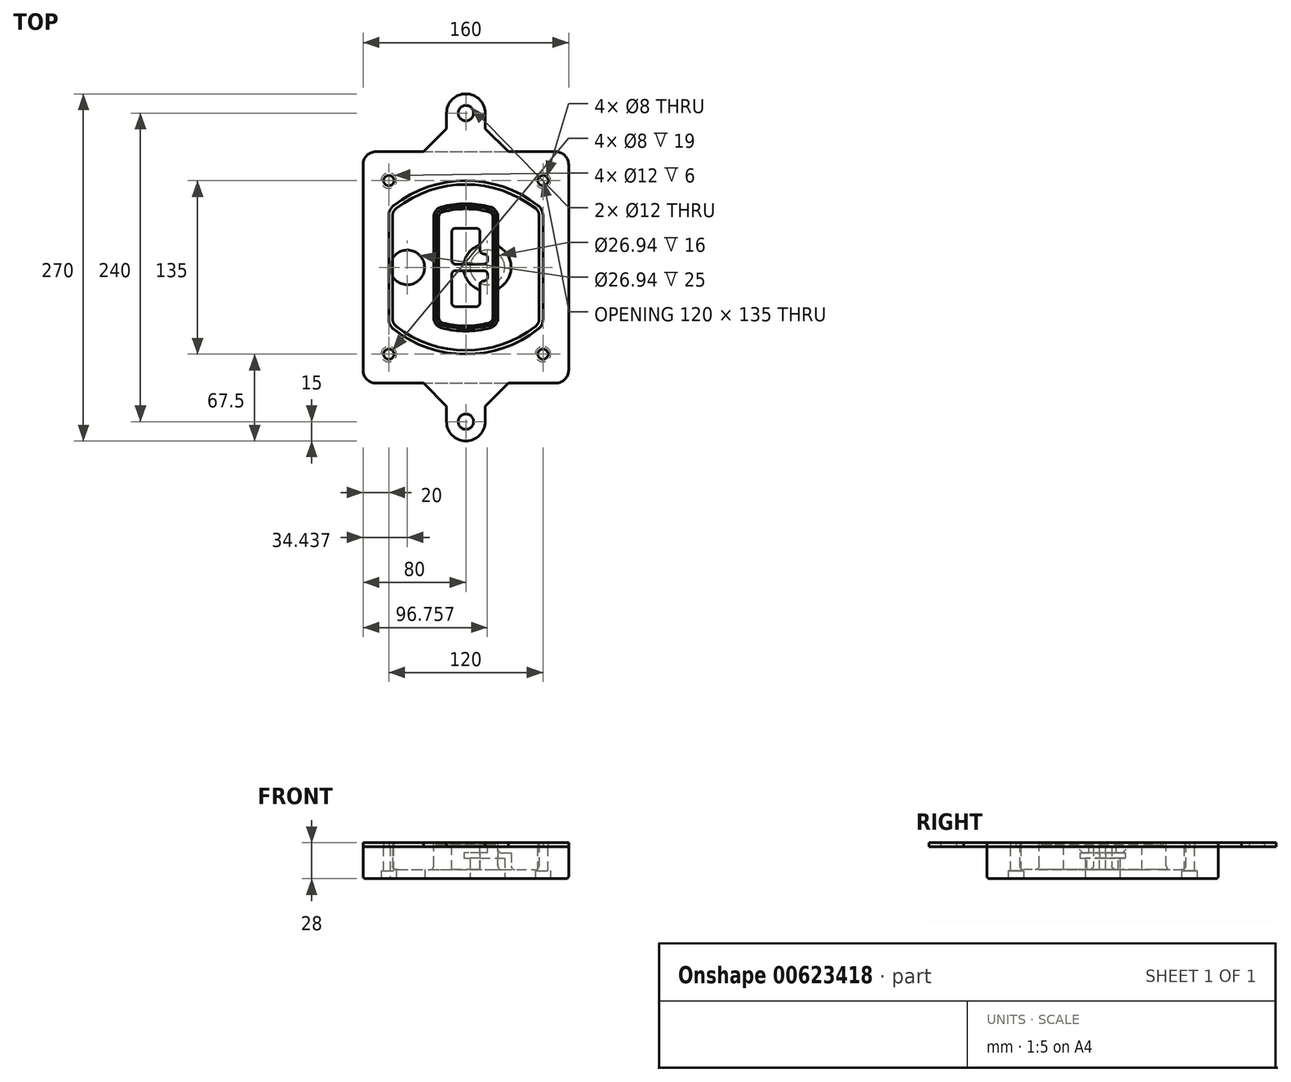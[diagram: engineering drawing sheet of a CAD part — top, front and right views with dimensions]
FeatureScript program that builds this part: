
annotation { "Feature Type Name" : "Feature", "Feature Type Description" : "" }
export const myFeature = defineFeature(function(context is Context, id is Id, definition is map)
    precondition{}
    {
        {
            var Q0;
            Q0=qCreatedBy(makeId("Top.planeOp"),FACE);
            var sketch = newSketch(context, id + "F0", { "sketchPlane" : qUnion([Q0])});
            skPoint(sketch, "E0.rect.middle", {"position": v(0, 0) * mm});
            skLineSegment(sketch, "E1.bottom", {"start": v(-70, -90) * mm, "end": v(70, -90) * mm});
            skLineSegment(sketch, "E1.top", {"start": v(-70, 90) * mm, "end": v(70, 90) * mm});
            skLineSegment(sketch, "E1.left", {"start": v(-80, -80) * mm, "end": v(-80, 80) * mm});
            skLineSegment(sketch, "E1.right", {"start": v(80, -80) * mm, "end": v(80, 80) * mm});
            skLineSegment(sketch, "E2", {"start": v(-80, 90) * mm, "end": v(80, -90) * mm, "construction": true});
            skLineSegment(sketch, "E3", {"start": v(80, 90) * mm, "end": v(-80, -90) * mm, "construction": true});
            skCircle(sketch, "E4", {"center": v(-60, 67.5) * mm, "radius": 4 * mm});
            skCircle(sketch, "E5", {"center": v(60, 67.5) * mm, "radius": 4 * mm});
            skCircle(sketch, "E6", {"center": v(60, -67.5) * mm, "radius": 4 * mm});
            skCircle(sketch, "E7", {"center": v(-60, -67.5) * mm, "radius": 4 * mm});
            skLineSegment(sketch, "E8", {"start": v(-60, 67.5) * mm, "end": v(60, 67.5) * mm, "construction": true});
            skLineSegment(sketch, "E9", {"start": v(60, 67.5) * mm, "end": v(60, -67.5) * mm, "construction": true});
            skLineSegment(sketch, "E10", {"start": v(60, -67.5) * mm, "end": v(-60, -67.5) * mm, "construction": true});
            skLineSegment(sketch, "E11", {"start": v(-60, -67.5) * mm, "end": v(-60, 67.5) * mm, "construction": true});
            skLineSegment(sketch, "E12", {"start": v(-60, 40.3) * mm, "end": v(-60, -40.3) * mm});
            skLineSegment(sketch, "E13", {"start": v(60, 40.3) * mm, "end": v(60, -40.3) * mm});
            skArc(sketch, "E14", {"start": v(56.15, 48.18) * mm, "mid": v(0, 67.5) * mm, "end": v(-56.15, 48.18) * mm});
            skArc(sketch, "E15", {"start": v(-56.15, -48.18) * mm, "mid": v(0, -67.5) * mm, "end": v(56.15, -48.18) * mm});
            skLineSegment(sketch, "E16", {"start": v(-60, 0) * mm, "end": v(60, 0) * mm, "construction": true});
            skPoint(sketch, "E17.visualSharp", {"position": v(-60, -45) * mm});
            skArc(sketch, "E17.filletArc", {"start": v(-60, -40.3) * mm, "mid": v(-58.99, -44.68) * mm, "end": v(-56.15, -48.18) * mm});
            skPoint(sketch, "E18.visualSharp", {"position": v(-60, 45) * mm});
            skArc(sketch, "E18.filletArc", {"start": v(-56.15, 48.18) * mm, "mid": v(-58.99, 44.68) * mm, "end": v(-60, 40.3) * mm});
            skPoint(sketch, "E19.visualSharp", {"position": v(60, 45) * mm});
            skArc(sketch, "E19.filletArc", {"start": v(60, 40.3) * mm, "mid": v(58.99, 44.68) * mm, "end": v(56.15, 48.18) * mm});
            skPoint(sketch, "E20.visualSharp", {"position": v(60, -45) * mm});
            skArc(sketch, "E20.filletArc", {"start": v(56.15, -48.18) * mm, "mid": v(58.99, -44.68) * mm, "end": v(60, -40.3) * mm});
            skPoint(sketch, "E21.visualSharp", {"position": v(-80, 90) * mm});
            skArc(sketch, "E21.filletArc", {"start": v(-70, 90) * mm, "mid": v(-77.07, 87.07) * mm, "end": v(-80, 80) * mm});
            skPoint(sketch, "E22.visualSharp", {"position": v(80, 90) * mm});
            skArc(sketch, "E22.filletArc", {"start": v(80, 80) * mm, "mid": v(77.07, 87.07) * mm, "end": v(70, 90) * mm});
            skPoint(sketch, "E23.visualSharp", {"position": v(80, -90) * mm});
            skArc(sketch, "E23.filletArc", {"start": v(70, -90) * mm, "mid": v(77.07, -87.07) * mm, "end": v(80, -80) * mm});
            skPoint(sketch, "E24.visualSharp", {"position": v(-80, -90) * mm});
            skArc(sketch, "E24.filletArc", {"start": v(-80, -80) * mm, "mid": v(-77.07, -87.07) * mm, "end": v(-70, -90) * mm});
            skArc(sketch, "E25.0", {"start": v(57, 40.3) * mm, "mid": v(56.3, 43.36) * mm, "end": v(54.3, 45.81) * mm});
            skLineSegment(sketch, "E25.1", {"start": v(57, 40.3) * mm, "end": v(57, -40.3) * mm});
            skArc(sketch, "E25.2", {"start": v(54.3, -45.81) * mm, "mid": v(56.3, -43.36) * mm, "end": v(57, -40.3) * mm});
            skArc(sketch, "E25.3", {"start": v(-54.3, -45.81) * mm, "mid": v(0, -64.5) * mm, "end": v(54.3, -45.81) * mm});
            skArc(sketch, "E25.4", {"start": v(-57, -40.3) * mm, "mid": v(-56.3, -43.36) * mm, "end": v(-54.3, -45.81) * mm});
            skArc(sketch, "E25.5", {"start": v(54.3, 45.81) * mm, "mid": v(0, 64.5) * mm, "end": v(-54.3, 45.81) * mm});
            skLineSegment(sketch, "E25.6", {"start": v(-57, 40.3) * mm, "end": v(-57, -40.3) * mm});
            skArc(sketch, "E25.7", {"start": v(-54.3, 45.81) * mm, "mid": v(-56.3, 43.36) * mm, "end": v(-57, 40.3) * mm});
            skArc(sketch, "E26.0", {"start": v(-58.62, 51.33) * mm, "mid": v(-62.58, 46.43) * mm, "end": v(-64, 40.3) * mm});
            skArc(sketch, "E26.1", {"start": v(58.62, 51.33) * mm, "mid": v(0, 71.5) * mm, "end": v(-58.62, 51.33) * mm});
            skArc(sketch, "E26.2", {"start": v(64, 40.3) * mm, "mid": v(62.58, 46.43) * mm, "end": v(58.62, 51.33) * mm});
            skLineSegment(sketch, "E26.3", {"start": v(64, 40.3) * mm, "end": v(64, -40.3) * mm});
            skArc(sketch, "E26.4", {"start": v(58.62, -51.33) * mm, "mid": v(62.58, -46.43) * mm, "end": v(64, -40.3) * mm});
            skLineSegment(sketch, "E26.5", {"start": v(-64, 40.3) * mm, "end": v(-64, -40.3) * mm});
            skArc(sketch, "E26.6", {"start": v(-58.62, -51.33) * mm, "mid": v(0, -71.5) * mm, "end": v(58.62, -51.33) * mm});
            skArc(sketch, "E26.7", {"start": v(-64, -40.3) * mm, "mid": v(-62.58, -46.43) * mm, "end": v(-58.62, -51.33) * mm});
            skSolve(sketch);
        }
        {
            var Q0;
            Q0=makeQuery(id+"F0.imprint","IMPRINT",FACE,{"disambiguationData":[TD([[makeQuery(id+"F0.imprint","IMPRINT",EDGE,{"derivedFrom":sQuery(id+"F0.wireOp",EDGE,"E1.bottom")}),1.0]])]});
            var Q1;
            Q1=makeQuery(id+"F0.imprint","IMPRINT",FACE,{"disambiguationData":[TD([[makeQuery(id+"F0.imprint","IMPRINT",EDGE,{"derivedFrom":sQuery(id+"F0.wireOp",EDGE,"E12")}),1.0]])]});
            var Q2;
            Q2=makeQuery(id+"F0.imprint","IMPRINT",FACE,{"disambiguationData":[TD([[makeQuery(id+"F0.imprint","IMPRINT",EDGE,{"derivedFrom":sQuery(id+"F0.wireOp",EDGE,"E25.0")}),1.0]])]});
            var Q3;
            Q3=makeQuery(id+"F0.imprint","IMPRINT",FACE,{"disambiguationData":[TD([[makeQuery(id+"F0.imprint","IMPRINT",EDGE,{"derivedFrom":sQuery(id+"F0.wireOp",EDGE,"E12")}),-1.0]])]});
            extrude(context, id + "F1", {"entities" : qUnion([Q0, Q1, Q2, Q3]), "oppositeDirection" : true, "depth" : 25 * mm});
        }
        {
            var Q0;
            Q0=makeQuery(id+"F0.imprint","IMPRINT",FACE,{"disambiguationData":[TD([[makeQuery(id+"F0.imprint","IMPRINT",EDGE,{"derivedFrom":sQuery(id+"F0.wireOp",EDGE,"E12")}),1.0]])]});
            extrude(context, id + "F2", {"entities" : qUnion([Q0]), "operationType" : NewBodyOperationType.ADD, "depth" : 3 * mm});
        }
        {
            var Q0;
            Q0=makeQuery(id+"F0.imprint","IMPRINT",FACE,{"disambiguationData":[TD([[makeQuery(id+"F0.imprint","IMPRINT",EDGE,{"derivedFrom":sQuery(id+"F0.wireOp",EDGE,"E25.0")}),1.0]])]});
            extrude(context, id + "F3", {"entities" : qUnion([Q0]), "operationType" : NewBodyOperationType.REMOVE, "oppositeDirection" : true, "depth" : 18 * mm});
        }
        {
            var Q0;
            Q0=makeQuery(id+"F2.opExtrude","CAP_FACE",FACE,{"disambiguationData":[OSD([sQuery(id+"F0.wireOp",EDGE,"E12"),sQuery(id+"F0.wireOp",EDGE,"E13"),sQuery(id+"F0.wireOp",EDGE,"E14"),sQuery(id+"F0.wireOp",EDGE,"E15"),sQuery(id+"F0.wireOp",EDGE,"E17.filletArc"),sQuery(id+"F0.wireOp",EDGE,"E18.filletArc"),sQuery(id+"F0.wireOp",EDGE,"E19.filletArc"),sQuery(id+"F0.wireOp",EDGE,"E20.filletArc"),sQuery(id+"F0.wireOp",EDGE,"E25.0"),sQuery(id+"F0.wireOp",EDGE,"E25.1"),sQuery(id+"F0.wireOp",EDGE,"E25.2"),sQuery(id+"F0.wireOp",EDGE,"E25.3"),sQuery(id+"F0.wireOp",EDGE,"E25.4"),sQuery(id+"F0.wireOp",EDGE,"E25.5"),sQuery(id+"F0.wireOp",EDGE,"E25.6"),sQuery(id+"F0.wireOp",EDGE,"E25.7")])],"isStart":false});
            var sketch = newSketch(context, id + "F4", { "sketchPlane" : qUnion([Q0])});
            skArc(sketch, "E27.0", {"start": v(-19.08, -46.97) * mm, "mid": v(0, -49.5) * mm, "end": v(19.08, -46.97) * mm});
            skArc(sketch, "E28.0", {"start": v(19.08, 46.97) * mm, "mid": v(0, 49.5) * mm, "end": v(-19.08, 46.97) * mm});
            skLineSegment(sketch, "E29", {"start": v(-25, 39.25) * mm, "end": v(-25, -39.25) * mm});
            skLineSegment(sketch, "E30", {"start": v(25, 39.25) * mm, "end": v(25, -39.25) * mm});
            skLineSegment(sketch, "E31", {"start": v(-25, 45.1) * mm, "end": v(25, 45.1) * mm, "construction": true});
            skLineSegment(sketch, "E32", {"start": v(-25, -45.1) * mm, "end": v(25, -45.1) * mm, "construction": true});
            skPoint(sketch, "E33.visualSharp", {"position": v(-25, 45.1) * mm});
            skArc(sketch, "E33.filletArc", {"start": v(-19.08, 46.97) * mm, "mid": v(-23.35, 44.11) * mm, "end": v(-25, 39.25) * mm});
            skPoint(sketch, "E34.visualSharp", {"position": v(25, 45.1) * mm});
            skArc(sketch, "E34.filletArc", {"start": v(25, 39.25) * mm, "mid": v(23.35, 44.11) * mm, "end": v(19.08, 46.97) * mm});
            skPoint(sketch, "E35.visualSharp", {"position": v(25, -45.1) * mm});
            skArc(sketch, "E35.filletArc", {"start": v(19.08, -46.97) * mm, "mid": v(23.35, -44.11) * mm, "end": v(25, -39.25) * mm});
            skPoint(sketch, "E36.visualSharp", {"position": v(-25, -45.1) * mm});
            skArc(sketch, "E36.filletArc", {"start": v(-25, -39.25) * mm, "mid": v(-23.35, -44.11) * mm, "end": v(-19.08, -46.97) * mm});
            skArc(sketch, "E37.0", {"start": v(54.3, 45.81) * mm, "mid": v(0, 64.5) * mm, "end": v(-54.3, 45.81) * mm});
            skArc(sketch, "E37.1", {"start": v(-54.3, 45.81) * mm, "mid": v(-56.3, 43.36) * mm, "end": v(-57, 40.3) * mm});
            skLineSegment(sketch, "E37.2", {"start": v(-57, 40.3) * mm, "end": v(-57, -40.3) * mm});
            skArc(sketch, "E37.3", {"start": v(-57, -40.3) * mm, "mid": v(-56.3, -43.36) * mm, "end": v(-54.3, -45.81) * mm});
            skArc(sketch, "E37.4", {"start": v(-54.3, -45.81) * mm, "mid": v(0, -64.5) * mm, "end": v(54.3, -45.81) * mm});
            skArc(sketch, "E37.5", {"start": v(54.3, -45.81) * mm, "mid": v(56.3, -43.36) * mm, "end": v(57, -40.3) * mm});
            skLineSegment(sketch, "E37.6", {"start": v(57, 40.3) * mm, "end": v(57, -40.3) * mm});
            skArc(sketch, "E37.7", {"start": v(57, 40.3) * mm, "mid": v(56.3, 43.36) * mm, "end": v(54.3, 45.81) * mm});
            skLineSegment(sketch, "E38.0", {"start": v(23, 39.25) * mm, "end": v(23, -39.25) * mm});
            skArc(sketch, "E38.1", {"start": v(18.56, -45.04) * mm, "mid": v(21.76, -42.9) * mm, "end": v(23, -39.25) * mm});
            skArc(sketch, "E38.2", {"start": v(-18.56, -45.04) * mm, "mid": v(0, -47.5) * mm, "end": v(18.56, -45.04) * mm});
            skArc(sketch, "E38.3", {"start": v(-23, -39.25) * mm, "mid": v(-21.76, -42.9) * mm, "end": v(-18.56, -45.04) * mm});
            skLineSegment(sketch, "E38.4", {"start": v(-23, 39.25) * mm, "end": v(-23, -39.25) * mm});
            skArc(sketch, "E38.5", {"start": v(23, 39.25) * mm, "mid": v(21.76, 42.9) * mm, "end": v(18.56, 45.04) * mm});
            skArc(sketch, "E38.6", {"start": v(-18.56, 45.04) * mm, "mid": v(-21.76, 42.9) * mm, "end": v(-23, 39.25) * mm});
            skArc(sketch, "E38.7", {"start": v(18.56, 45.04) * mm, "mid": v(0, 47.5) * mm, "end": v(-18.56, 45.04) * mm});
            skArc(sketch, "E39.0", {"start": v(21, 39.25) * mm, "mid": v(20.18, 41.68) * mm, "end": v(18.04, 43.1) * mm});
            skLineSegment(sketch, "E39.1", {"start": v(21, 39.25) * mm, "end": v(21, -39.25) * mm});
            skArc(sketch, "E39.2", {"start": v(18.04, -43.1) * mm, "mid": v(20.18, -41.68) * mm, "end": v(21, -39.25) * mm});
            skArc(sketch, "E39.3", {"start": v(-18.04, -43.1) * mm, "mid": v(0, -45.5) * mm, "end": v(18.04, -43.1) * mm});
            skArc(sketch, "E39.4", {"start": v(-21, -39.25) * mm, "mid": v(-20.18, -41.68) * mm, "end": v(-18.04, -43.1) * mm});
            skArc(sketch, "E39.5", {"start": v(18.04, 43.1) * mm, "mid": v(0, 45.5) * mm, "end": v(-18.04, 43.1) * mm});
            skLineSegment(sketch, "E39.6", {"start": v(-21, 39.25) * mm, "end": v(-21, -39.25) * mm});
            skArc(sketch, "E39.7", {"start": v(-18.04, 43.1) * mm, "mid": v(-20.18, 41.68) * mm, "end": v(-21, 39.25) * mm});
            skLineSegment(sketch, "E40", {"start": v(-25, 0) * mm, "end": v(25, 0) * mm, "construction": true});
            skLineSegment(sketch, "E41", {"start": v(-11, 5.5) * mm, "end": v(-11, 27.5) * mm});
            skLineSegment(sketch, "E42", {"start": v(-8, 30.5) * mm, "end": v(8, 30.5) * mm});
            skLineSegment(sketch, "E43", {"start": v(11, 27.5) * mm, "end": v(11, 13.5) * mm});
            skLineSegment(sketch, "E44", {"start": v(14, 10.5) * mm, "end": v(14, 10.5) * mm});
            skLineSegment(sketch, "E45", {"start": v(17, 7.5) * mm, "end": v(17, 5.5) * mm});
            skLineSegment(sketch, "E46", {"start": v(14, 2.5) * mm, "end": v(-8, 2.5) * mm});
            skPoint(sketch, "E47.visualSharp", {"position": v(-11, 30.5) * mm});
            skArc(sketch, "E47.filletArc", {"start": v(-8, 30.5) * mm, "mid": v(-10.12, 29.62) * mm, "end": v(-11, 27.5) * mm});
            skPoint(sketch, "E48.visualSharp", {"position": v(11, 30.5) * mm});
            skArc(sketch, "E48.filletArc", {"start": v(11, 27.5) * mm, "mid": v(10.12, 29.62) * mm, "end": v(8, 30.5) * mm});
            skPoint(sketch, "E49.visualSharp", {"position": v(11, 10.5) * mm});
            skArc(sketch, "E49.filletArc", {"start": v(11, 13.5) * mm, "mid": v(11.88, 11.38) * mm, "end": v(14, 10.5) * mm});
            skPoint(sketch, "E50.visualSharp", {"position": v(17, 10.5) * mm});
            skArc(sketch, "E50.filletArc", {"start": v(17, 7.5) * mm, "mid": v(16.12, 9.62) * mm, "end": v(14, 10.5) * mm});
            skPoint(sketch, "E51.visualSharp", {"position": v(17, 2.5) * mm});
            skArc(sketch, "E51.filletArc", {"start": v(14, 2.5) * mm, "mid": v(16.12, 3.38) * mm, "end": v(17, 5.5) * mm});
            skPoint(sketch, "E52.visualSharp", {"position": v(-11, 2.5) * mm});
            skArc(sketch, "E52.filletArc", {"start": v(-11, 5.5) * mm, "mid": v(-10.12, 3.38) * mm, "end": v(-8, 2.5) * mm});
            skLineSegment(sketch, "E53.0.MirrorCS", {"start": v(14, -2.5) * mm, "end": v(-8, -2.5) * mm});
            skArc(sketch, "E54.0.MirrorCS", {"start": v(-11, -5.5) * mm, "mid": v(-10.12, -3.38) * mm, "end": v(-8, -2.5) * mm});
            skLineSegment(sketch, "E55.0.MirrorCS", {"start": v(-11, -5.5) * mm, "end": v(-11, -27.5) * mm});
            skArc(sketch, "E56.0.MirrorCS", {"start": v(-8, -30.5) * mm, "mid": v(-10.12, -29.62) * mm, "end": v(-11, -27.5) * mm});
            skLineSegment(sketch, "E57.0.MirrorCS", {"start": v(-8, -30.5) * mm, "end": v(8, -30.5) * mm});
            skArc(sketch, "E58.0.MirrorCS", {"start": v(11, -27.5) * mm, "mid": v(10.12, -29.62) * mm, "end": v(8, -30.5) * mm});
            skLineSegment(sketch, "E59.0.MirrorCS", {"start": v(11, -27.5) * mm, "end": v(11, -13.5) * mm});
            skArc(sketch, "E60.0.MirrorCS", {"start": v(11, -13.5) * mm, "mid": v(11.88, -11.38) * mm, "end": v(14, -10.5) * mm});
            skArc(sketch, "E61.0.MirrorCS", {"start": v(17, -7.5) * mm, "mid": v(16.12, -9.62) * mm, "end": v(14, -10.5) * mm});
            skLineSegment(sketch, "E62.0.MirrorCS", {"start": v(17, -7.5) * mm, "end": v(17, -5.5) * mm});
            skArc(sketch, "E63.0.MirrorCS", {"start": v(14, -2.5) * mm, "mid": v(16.12, -3.38) * mm, "end": v(17, -5.5) * mm});
            skSolve(sketch);
        }
        {
            var Q0;
            Q0=makeQuery(id+"F4.imprint","IMPRINT",FACE,{"disambiguationData":[TD([[makeQuery(id+"F4.imprint","IMPRINT",EDGE,{"derivedFrom":sQuery(id+"F4.wireOp",EDGE,"E27.0")}),1.0]])]});
            var Q1;
            Q1=makeQuery(id+"F4.imprint","IMPRINT",FACE,{"disambiguationData":[TD([[makeQuery(id+"F4.imprint","IMPRINT",EDGE,{"derivedFrom":sQuery(id+"F4.wireOp",EDGE,"E38.0")}),-1.0]])]});
            var Q2;
            Q2=makeQuery(id+"F4.imprint","IMPRINT",FACE,{"disambiguationData":[TD([[makeQuery(id+"F4.imprint","IMPRINT",EDGE,{"derivedFrom":sQuery(id+"F4.wireOp",EDGE,"E39.0")}),1.0]])]});
            extrude(context, id + "F5", {"entities" : qUnion([Q0, Q1, Q2]), "operationType" : NewBodyOperationType.ADD, "endBound" : BoundingType.UP_TO_NEXT, "oppositeDirection" : true, "depth" : 25 * mm});
        }
        {
            var Q0;
            Q0=makeQuery(id+"F4.imprint","IMPRINT",FACE,{"disambiguationData":[TD([[makeQuery(id+"F4.imprint","IMPRINT",EDGE,{"derivedFrom":sQuery(id+"F4.wireOp",EDGE,"E38.0")}),-1.0]])]});
            extrude(context, id + "F6", {"entities" : qUnion([Q0]), "operationType" : NewBodyOperationType.REMOVE, "oppositeDirection" : true, "depth" : 2 * mm});
        }
        {
            var Q0;
            Q0=makeQuery(id+"F1.opExtrude","CAP_FACE",FACE,{"disambiguationData":[OSD([sQuery(id+"F0.wireOp",EDGE,"E1.bottom"),sQuery(id+"F0.wireOp",EDGE,"E1.top"),sQuery(id+"F0.wireOp",EDGE,"E1.left"),sQuery(id+"F0.wireOp",EDGE,"E1.right"),sQuery(id+"F0.wireOp",EDGE,"E4"),sQuery(id+"F0.wireOp",EDGE,"E5"),sQuery(id+"F0.wireOp",EDGE,"E6"),sQuery(id+"F0.wireOp",EDGE,"E7"),sQuery(id+"F0.wireOp",EDGE,"E21.filletArc"),sQuery(id+"F0.wireOp",EDGE,"E22.filletArc"),sQuery(id+"F0.wireOp",EDGE,"E23.filletArc"),sQuery(id+"F0.wireOp",EDGE,"E24.filletArc")])],"isStart":false});
            var sketch = newSketch(context, id + "F7", { "sketchPlane" : qUnion([Q0])});
            skCircle(sketch, "E64", {"center": v(16.76, 0) * mm, "radius": 13.47 * mm});
            skCircle(sketch, "E65", {"center": v(-45.56, 0) * mm, "radius": 13.47 * mm});
            skLineSegment(sketch, "E66", {"start": v(80, 0) * mm, "end": v(-80, 0) * mm});
            skCircle(sketch, "E67", {"center": v(16.76, 0) * mm, "radius": 18.47 * mm});
            skCircle(sketch, "E68", {"center": v(60, -67.5) * mm, "radius": 6 * mm});
            skCircle(sketch, "E69", {"center": v(-60, -67.5) * mm, "radius": 6 * mm});
            skCircle(sketch, "E70", {"center": v(-60, 67.5) * mm, "radius": 6 * mm});
            skCircle(sketch, "E71", {"center": v(60, 67.5) * mm, "radius": 6 * mm});
            skSolve(sketch);
        }
        {
            var Q0;
            {var subQ1=sQuery(id+"F7.wireOp",EDGE,"E66");var subQ4=sQuery(id+"F7.wireOp",EDGE,"E64");var subQ6=makeQuery(id+"F7.imprint","INTERSECT",VERTEX,{"disambiguationData":[OD(0.0)],"derivedFrom":[subQ4,subQ1]});Q0=makeQuery(id+"F7.imprint","IMPRINT",FACE,{"disambiguationData":[TD([[makeQuery(id+"F7.imprint","IMPRINT",EDGE,{"disambiguationData":[TD([[subQ6,-1.0]])],"derivedFrom":subQ4}),-1.0]])]});}
            var Q1;
            {var subQ0=sQuery(id+"F7.wireOp",EDGE,"E66");var subQ1=sQuery(id+"F7.wireOp",EDGE,"E64");var subQ3=makeQuery(id+"F7.imprint","INTERSECT",VERTEX,{"disambiguationData":[OD(0.0)],"derivedFrom":[subQ1,subQ0]});Q1=makeQuery(id+"F7.imprint","IMPRINT",FACE,{"disambiguationData":[TD([[makeQuery(id+"F7.imprint","IMPRINT",EDGE,{"disambiguationData":[TD([[subQ3,-1.0]])],"derivedFrom":subQ1}),1.0]])]});}
            var Q2;
            {var subQ0=sQuery(id+"F7.wireOp",EDGE,"E66");var subQ1=sQuery(id+"F7.wireOp",EDGE,"E64");var subQ3=makeQuery(id+"F7.imprint","INTERSECT",VERTEX,{"disambiguationData":[OD(0.0)],"derivedFrom":[subQ1,subQ0]});Q2=makeQuery(id+"F7.imprint","IMPRINT",FACE,{"disambiguationData":[TD([[makeQuery(id+"F7.imprint","IMPRINT",EDGE,{"disambiguationData":[TD([[subQ3,1.0]])],"derivedFrom":subQ1}),1.0]])]});}
            var Q3;
            {var subQ1=sQuery(id+"F7.wireOp",EDGE,"E66");var subQ4=sQuery(id+"F7.wireOp",EDGE,"E64");var subQ6=makeQuery(id+"F7.imprint","INTERSECT",VERTEX,{"disambiguationData":[OD(0.0)],"derivedFrom":[subQ4,subQ1]});Q3=makeQuery(id+"F7.imprint","IMPRINT",FACE,{"disambiguationData":[TD([[makeQuery(id+"F7.imprint","IMPRINT",EDGE,{"disambiguationData":[TD([[subQ6,1.0]])],"derivedFrom":subQ4}),-1.0]])]});}
            extrude(context, id + "F8", {"entities" : qUnion([Q0, Q1, Q2, Q3]), "operationType" : NewBodyOperationType.ADD, "oppositeDirection" : true, "depth" : 20 * mm});
        }
        {
            var Q0;
            {var subQ0=sQuery(id+"F7.wireOp",EDGE,"E66");var subQ1=sQuery(id+"F7.wireOp",EDGE,"E64");var subQ3=makeQuery(id+"F7.imprint","INTERSECT",VERTEX,{"disambiguationData":[OD(0.0)],"derivedFrom":[subQ1,subQ0]});Q0=makeQuery(id+"F7.imprint","IMPRINT",FACE,{"disambiguationData":[TD([[makeQuery(id+"F7.imprint","IMPRINT",EDGE,{"disambiguationData":[TD([[subQ3,-1.0]])],"derivedFrom":subQ1}),1.0]])]});}
            var Q1;
            {var subQ0=sQuery(id+"F7.wireOp",EDGE,"E66");var subQ1=sQuery(id+"F7.wireOp",EDGE,"E64");var subQ3=makeQuery(id+"F7.imprint","INTERSECT",VERTEX,{"disambiguationData":[OD(0.0)],"derivedFrom":[subQ1,subQ0]});Q1=makeQuery(id+"F7.imprint","IMPRINT",FACE,{"disambiguationData":[TD([[makeQuery(id+"F7.imprint","IMPRINT",EDGE,{"disambiguationData":[TD([[subQ3,1.0]])],"derivedFrom":subQ1}),1.0]])]});}
            extrude(context, id + "F9", {"entities" : qUnion([Q0, Q1]), "operationType" : NewBodyOperationType.REMOVE, "oppositeDirection" : true, "depth" : 16 * mm});
        }
        {
            var Q0;
            {var subQ0=sQuery(id+"F7.wireOp",EDGE,"E66");var subQ1=sQuery(id+"F7.wireOp",EDGE,"E65");var subQ3=makeQuery(id+"F7.imprint","INTERSECT",VERTEX,{"disambiguationData":[OD(0.0)],"derivedFrom":[subQ1,subQ0]});Q0=makeQuery(id+"F7.imprint","IMPRINT",FACE,{"disambiguationData":[TD([[makeQuery(id+"F7.imprint","IMPRINT",EDGE,{"disambiguationData":[TD([[subQ3,-1.0]])],"derivedFrom":subQ1}),1.0]])]});}
            var Q1;
            {var subQ0=sQuery(id+"F7.wireOp",EDGE,"E66");var subQ1=sQuery(id+"F7.wireOp",EDGE,"E65");var subQ3=makeQuery(id+"F7.imprint","INTERSECT",VERTEX,{"disambiguationData":[OD(0.0)],"derivedFrom":[subQ1,subQ0]});Q1=makeQuery(id+"F7.imprint","IMPRINT",FACE,{"disambiguationData":[TD([[makeQuery(id+"F7.imprint","IMPRINT",EDGE,{"disambiguationData":[TD([[subQ3,1.0]])],"derivedFrom":subQ1}),1.0]])]});}
            extrude(context, id + "F10", {"entities" : qUnion([Q0, Q1]), "operationType" : NewBodyOperationType.REMOVE, "oppositeDirection" : true, "depth" : 25 * mm});
        }
        {
            var Q0;
            Q0=makeQuery(id+"F7.imprint","IMPRINT",FACE,{"disambiguationData":[TD([[makeQuery(id+"F7.imprint","IMPRINT",EDGE,{"derivedFrom":sQuery(id+"F7.wireOp",EDGE,"E68")}),1.0]])]});
            var Q1;
            Q1=makeQuery(id+"F7.imprint","IMPRINT",FACE,{"disambiguationData":[TD([[makeQuery(id+"F7.imprint","IMPRINT",EDGE,{"derivedFrom":makeQuery(id+"F1.opExtrude","CAP_EDGE",EDGE,{"disambiguationData":[OSD([sQuery(id+"F0.wireOp",EDGE,"E5")])],"isStart":false})}),-1.0]])]});
            var Q2;
            Q2=makeQuery(id+"F7.imprint","IMPRINT",FACE,{"disambiguationData":[TD([[makeQuery(id+"F7.imprint","IMPRINT",EDGE,{"derivedFrom":sQuery(id+"F7.wireOp",EDGE,"E69")}),1.0]])]});
            var Q3;
            Q3=makeQuery(id+"F7.imprint","IMPRINT",FACE,{"disambiguationData":[TD([[makeQuery(id+"F7.imprint","IMPRINT",EDGE,{"derivedFrom":makeQuery(id+"F1.opExtrude","CAP_EDGE",EDGE,{"disambiguationData":[OSD([sQuery(id+"F0.wireOp",EDGE,"E4")])],"isStart":false})}),-1.0]])]});
            var Q4;
            Q4=makeQuery(id+"F7.imprint","IMPRINT",FACE,{"disambiguationData":[TD([[makeQuery(id+"F7.imprint","IMPRINT",EDGE,{"derivedFrom":sQuery(id+"F7.wireOp",EDGE,"E70")}),1.0]])]});
            var Q5;
            Q5=makeQuery(id+"F7.imprint","IMPRINT",FACE,{"disambiguationData":[TD([[makeQuery(id+"F7.imprint","IMPRINT",EDGE,{"derivedFrom":makeQuery(id+"F1.opExtrude","CAP_EDGE",EDGE,{"disambiguationData":[OSD([sQuery(id+"F0.wireOp",EDGE,"E7")])],"isStart":false})}),-1.0]])]});
            var Q6;
            Q6=makeQuery(id+"F7.imprint","IMPRINT",FACE,{"disambiguationData":[TD([[makeQuery(id+"F7.imprint","IMPRINT",EDGE,{"derivedFrom":sQuery(id+"F7.wireOp",EDGE,"E71")}),1.0]])]});
            var Q7;
            Q7=makeQuery(id+"F7.imprint","IMPRINT",FACE,{"disambiguationData":[TD([[makeQuery(id+"F7.imprint","IMPRINT",EDGE,{"derivedFrom":makeQuery(id+"F1.opExtrude","CAP_EDGE",EDGE,{"disambiguationData":[OSD([sQuery(id+"F0.wireOp",EDGE,"E6")])],"isStart":false})}),-1.0]])]});
            extrude(context, id + "F11", {"entities" : qUnion([Q0, Q1, Q2, Q3, Q4, Q5, Q6, Q7]), "operationType" : NewBodyOperationType.REMOVE, "oppositeDirection" : true, "depth" : 6 * mm});
        }
        {
            var Q0;
            Q0=makeQuery(id+"F9.boolean.opBoolean","COPY",FACE,{"derivedFrom":makeQuery(id+"F9.opExtrude","CAP_FACE",FACE,{"disambiguationData":[OSD([sQuery(id+"F7.wireOp",EDGE,"E64")])],"isStart":false})});
            var sketch = newSketch(context, id + "F12", { "sketchPlane" : qUnion([Q0])});
            skArc(sketch, "E72.0", {"start": v(11, 17.55) * mm, "mid": v(2.57, 11.82) * mm, "end": v(-1.54, 2.5) * mm});
            skArc(sketch, "E72.1", {"start": v(-1.54, -2.5) * mm, "mid": v(2.57, -11.82) * mm, "end": v(11, -17.55) * mm});
            skLineSegment(sketch, "E73", {"start": v(-1.54, -2.5) * mm, "end": v(14, -2.5) * mm});
            skLineSegment(sketch, "E74.0", {"start": v(14, 2.5) * mm, "end": v(-1.54, 2.5) * mm});
            skArc(sketch, "E74.1", {"start": v(14, 2.5) * mm, "mid": v(16.12, 3.38) * mm, "end": v(17, 5.5) * mm});
            skLineSegment(sketch, "E74.2", {"start": v(17, 7.5) * mm, "end": v(17, 5.5) * mm});
            skArc(sketch, "E74.3", {"start": v(17, 7.5) * mm, "mid": v(16.12, 9.62) * mm, "end": v(14, 10.5) * mm});
            skArc(sketch, "E74.4", {"start": v(11, 13.5) * mm, "mid": v(11.88, 11.38) * mm, "end": v(14, 10.5) * mm});
            skLineSegment(sketch, "E74.5", {"start": v(11, 17.55) * mm, "end": v(11, 13.5) * mm});
            skLineSegment(sketch, "E74.7", {"start": v(14, -2.5) * mm, "end": v(-1.54, -2.5) * mm});
            skArc(sketch, "E74.8", {"start": v(14, -2.5) * mm, "mid": v(16.12, -3.38) * mm, "end": v(17, -5.5) * mm});
            skLineSegment(sketch, "E74.9", {"start": v(17, -7.5) * mm, "end": v(17, -5.5) * mm});
            skArc(sketch, "E74.10", {"start": v(17, -7.5) * mm, "mid": v(16.12, -9.62) * mm, "end": v(14, -10.5) * mm});
            skArc(sketch, "E74.11", {"start": v(11, -13.5) * mm, "mid": v(11.88, -11.38) * mm, "end": v(14, -10.5) * mm});
            skLineSegment(sketch, "E74.12", {"start": v(11, -17.55) * mm, "end": v(11, -13.5) * mm});
            skPoint(sketch, "E75.orphan", {"position": v(11, -27.5) * mm});
            skPoint(sketch, "E76.orphan", {"position": v(-8, -2.5) * mm});
            skPoint(sketch, "E77.orphan", {"position": v(-8, 2.5) * mm});
            skPoint(sketch, "E78.orphan", {"position": v(11, 27.5) * mm});
            skSolve(sketch);
        }
        {
            var Q0;
            {var subQ7=sQuery(id+"F12.wireOp",EDGE,"E72.0");var subQ14=sQuery(id+"F12.wireOp",EDGE,"E72.1");var subQ16=sQuery(id+"F12.wireOp",EDGE,"E74.1");var subQ18=sQuery(id+"F12.wireOp",EDGE,"E74.8");Q0=qUnion([makeQuery(id+"F12.imprint","IMPRINT",FACE,{"disambiguationData":[TD([[makeQuery(id+"F12.imprint","IMPRINT",EDGE,{"derivedFrom":subQ7}),1.0]])]}),makeQuery(id+"F12.imprint","IMPRINT",FACE,{"disambiguationData":[TD([[makeQuery(id+"F12.imprint","IMPRINT",EDGE,{"derivedFrom":subQ14}),1.0]])]}),makeQuery(id+"F12.imprint","IMPRINT",FACE,{"disambiguationData":[TD([[makeQuery(id+"F12.imprint","IMPRINT",EDGE,{"derivedFrom":subQ16}),1.0]])]}),makeQuery(id+"F12.imprint","IMPRINT",FACE,{"disambiguationData":[TD([[makeQuery(id+"F12.imprint","IMPRINT",EDGE,{"derivedFrom":subQ18}),-1.0]])]})]);}
            var Q1;
            Q1=makeQuery(id+"F5.boolean.opBoolean","SPLIT",FACE,{"disambiguationData":[TD([makeQuery(id+"F5.opExtrude","SWEPT_FACE",FACE,{"disambiguationData":[OSD([sQuery(id+"F4.wireOp",EDGE,"E41")])]})])],"derivedFrom":makeQuery(id+"F3.boolean.opBoolean","COPY",FACE,{"derivedFrom":makeQuery(id+"F3.opExtrude","CAP_FACE",FACE,{"disambiguationData":[OSD([sQuery(id+"F0.wireOp",EDGE,"E25.0"),sQuery(id+"F0.wireOp",EDGE,"E25.1"),sQuery(id+"F0.wireOp",EDGE,"E25.2"),sQuery(id+"F0.wireOp",EDGE,"E25.3"),sQuery(id+"F0.wireOp",EDGE,"E25.4"),sQuery(id+"F0.wireOp",EDGE,"E25.5"),sQuery(id+"F0.wireOp",EDGE,"E25.6"),sQuery(id+"F0.wireOp",EDGE,"E25.7")])],"isStart":false})})});
            extrude(context, id + "F13", {"entities" : qUnion([Q0]), "operationType" : NewBodyOperationType.REMOVE, "endBound" : BoundingType.UP_TO_SURFACE, "endBoundEntityFace" : qUnion([Q1]), "depth" : 25 * mm});
        }
        {
            var Q0;
            Q0=makeQuery(id+"F3.boolean.opBoolean","COPY",EDGE,{"derivedFrom":makeQuery(id+"F3.opExtrude","CAP_EDGE",EDGE,{"disambiguationData":[OSD([sQuery(id+"F0.wireOp",EDGE,"E25.6")])],"isStart":false})});
            var Q1;
            Q1=makeQuery(id+"F8.boolean.opBoolean","INTERSECT",EDGE,{"derivedFrom":[makeQuery(id+"F5.opExtrude","SWEPT_FACE",FACE,{"disambiguationData":[OSD([sQuery(id+"F4.wireOp",EDGE,"E30")])]}),makeQuery(id+"F8.opExtrude","CAP_FACE",FACE,{"disambiguationData":[OSD([sQuery(id+"F7.wireOp",EDGE,"E67")])],"isStart":false})]});
            var Q2;
            Q2=makeQuery(id+"F8.boolean.opBoolean","INTERSECT",EDGE,{"disambiguationData":[OD(1.0)],"derivedFrom":[makeQuery(id+"F5.opExtrude","SWEPT_FACE",FACE,{"disambiguationData":[OSD([sQuery(id+"F4.wireOp",EDGE,"E30")])]}),makeQuery(id+"F8.opExtrude","SWEPT_FACE",FACE,{"disambiguationData":[OSD([sQuery(id+"F7.wireOp",EDGE,"E67")])]})]});
            var Q3;
            {var subQ0=sQuery(id+"F4.wireOp",EDGE,"E30");Q3=makeQuery(id+"F8.boolean.opBoolean","SPLIT",EDGE,{"disambiguationData":[TD([makeQuery(id+"F5.opExtrude","SWEPT_FACE",FACE,{"disambiguationData":[OSD([sQuery(id+"F4.wireOp",EDGE,"E35.filletArc")])]})])],"derivedFrom":makeQuery(id+"F5.opExtrude","CAP_EDGE",EDGE,{"disambiguationData":[OSD([subQ0])],"isStart":false})});}
            var Q4;
            {var subQ0=sQuery(id+"F0.wireOp",EDGE,"E25.7");var subQ1=sQuery(id+"F0.wireOp",EDGE,"E25.1");var subQ2=sQuery(id+"F0.wireOp",EDGE,"E25.6");var subQ3=sQuery(id+"F0.wireOp",EDGE,"E25.5");var subQ4=sQuery(id+"F0.wireOp",EDGE,"E25.4");var subQ5=sQuery(id+"F0.wireOp",EDGE,"E25.0");var subQ6=sQuery(id+"F0.wireOp",EDGE,"E25.2");var subQ7=sQuery(id+"F0.wireOp",EDGE,"E25.3");Q4=makeQuery(id+"F8.boolean.opBoolean","INTERSECT",EDGE,{"derivedFrom":[makeQuery(id+"F5.boolean.opBoolean","SPLIT",FACE,{"disambiguationData":[TD([makeQuery(id+"F2.opExtrude","SWEPT_FACE",FACE,{"disambiguationData":[OSD([subQ5])]})])],"derivedFrom":makeQuery(id+"F3.boolean.opBoolean","COPY",FACE,{"derivedFrom":makeQuery(id+"F3.opExtrude","CAP_FACE",FACE,{"disambiguationData":[OSD([subQ5,subQ1,subQ6,subQ7,subQ4,subQ3,subQ2,subQ0])],"isStart":false})})}),makeQuery(id+"F8.opExtrude","SWEPT_FACE",FACE,{"disambiguationData":[OSD([sQuery(id+"F7.wireOp",EDGE,"E67")])]})]});}
            var Q5;
            Q5=makeQuery(id+"F8.boolean.opBoolean","INTERSECT",EDGE,{"disambiguationData":[OD(0.0)],"derivedFrom":[makeQuery(id+"F5.opExtrude","SWEPT_FACE",FACE,{"disambiguationData":[OSD([sQuery(id+"F4.wireOp",EDGE,"E30")])]}),makeQuery(id+"F8.opExtrude","SWEPT_FACE",FACE,{"disambiguationData":[OSD([sQuery(id+"F7.wireOp",EDGE,"E67")])]})]});
            fillet(context, id + "F14", {"entities" : qUnion([Q0, Q1, Q2, Q3, Q4, Q5]), "radius" : 3 * mm, "tangentPropagation" : true, "allowEdgeOverflow" : false});
        }
        {
            var Q0;
            Q0=makeQuery(id+"F1.opExtrude","CAP_EDGE",EDGE,{"disambiguationData":[OSD([sQuery(id+"F0.wireOp",EDGE,"E1.bottom")])],"isStart":false});
            fillet(context, id + "F15", {"entities" : qUnion([Q0]), "radius" : 2 * mm, "tangentPropagation" : true, "allowEdgeOverflow" : false});
        }
        {
            var Q0;
            {var subQ0=sQuery(id+"F0.wireOp",EDGE,"E21.filletArc");var subQ1=sQuery(id+"F0.wireOp",EDGE,"E7");var subQ2=sQuery(id+"F0.wireOp",EDGE,"E6");var subQ3=sQuery(id+"F0.wireOp",EDGE,"E5");var subQ4=sQuery(id+"F0.wireOp",EDGE,"E4");var subQ5=sQuery(id+"F0.wireOp",EDGE,"E22.filletArc");var subQ6=sQuery(id+"F0.wireOp",EDGE,"E1.bottom");var subQ7=sQuery(id+"F0.wireOp",EDGE,"E1.right");var subQ8=sQuery(id+"F0.wireOp",EDGE,"E1.top");var subQ9=sQuery(id+"F0.wireOp",EDGE,"E1.left");var subQ10=sQuery(id+"F0.wireOp",EDGE,"E23.filletArc");var subQ11=sQuery(id+"F0.wireOp",EDGE,"E24.filletArc");Q0=makeQuery(id+"F2.boolean.opBoolean","SPLIT",FACE,{"disambiguationData":[TD([makeQuery(id+"F1.opExtrude","SWEPT_FACE",FACE,{"disambiguationData":[OSD([subQ6])]})])],"derivedFrom":makeQuery(id+"F1.opExtrude","CAP_FACE",FACE,{"disambiguationData":[OSD([subQ6,subQ8,subQ9,subQ7,subQ4,subQ3,subQ2,subQ1,subQ0,subQ5,subQ10,subQ11])],"isStart":true})});}
            var sketch = newSketch(context, id + "F16", { "sketchPlane" : qUnion([Q0])});
            skLineSegment(sketch, "E79.0", {"start": v(-70, 90) * mm, "end": v(70, 90) * mm});
            skArc(sketch, "E79.1", {"start": v(-70, 90) * mm, "mid": v(-77.07, 87.07) * mm, "end": v(-80, 80) * mm});
            skLineSegment(sketch, "E79.2", {"start": v(-80, -80) * mm, "end": v(-80, 80) * mm});
            skArc(sketch, "E79.3", {"start": v(-80, -80) * mm, "mid": v(-77.07, -87.07) * mm, "end": v(-70, -90) * mm});
            skLineSegment(sketch, "E79.4", {"start": v(-70, -90) * mm, "end": v(70, -90) * mm});
            skArc(sketch, "E79.5", {"start": v(70, -90) * mm, "mid": v(77.07, -87.07) * mm, "end": v(80, -80) * mm});
            skLineSegment(sketch, "E79.6", {"start": v(80, -80) * mm, "end": v(80, 80) * mm});
            skArc(sketch, "E79.7", {"start": v(80, 80) * mm, "mid": v(77.07, 87.07) * mm, "end": v(70, 90) * mm});
            skCircle(sketch, "E79.8", {"center": v(-60, -67.5) * mm, "radius": 4 * mm});
            skCircle(sketch, "E79.9", {"center": v(-60, 67.5) * mm, "radius": 4 * mm});
            skCircle(sketch, "E79.10", {"center": v(60, 67.5) * mm, "radius": 4 * mm});
            skCircle(sketch, "E79.11", {"center": v(60, -67.5) * mm, "radius": 4 * mm});
            skArc(sketch, "E79.12", {"start": v(56.15, 48.18) * mm, "mid": v(0, 67.5) * mm, "end": v(-56.15, 48.18) * mm});
            skArc(sketch, "E79.13", {"start": v(-56.15, 48.18) * mm, "mid": v(-58.99, 44.68) * mm, "end": v(-60, 40.3) * mm});
            skLineSegment(sketch, "E79.14", {"start": v(-60, 40.3) * mm, "end": v(-60, -40.3) * mm});
            skArc(sketch, "E79.15", {"start": v(-60, -40.3) * mm, "mid": v(-58.99, -44.68) * mm, "end": v(-56.15, -48.18) * mm});
            skArc(sketch, "E79.16", {"start": v(-56.15, -48.18) * mm, "mid": v(0, -67.5) * mm, "end": v(56.15, -48.18) * mm});
            skArc(sketch, "E79.17", {"start": v(56.15, -48.18) * mm, "mid": v(58.99, -44.68) * mm, "end": v(60, -40.3) * mm});
            skLineSegment(sketch, "E79.18", {"start": v(60, 40.3) * mm, "end": v(60, -40.3) * mm});
            skArc(sketch, "E79.19", {"start": v(60, 40.3) * mm, "mid": v(58.99, 44.68) * mm, "end": v(56.15, 48.18) * mm});
            skLineSegment(sketch, "E80", {"start": v(0, 90) * mm, "end": v(0, 120) * mm, "construction": true});
            skCircle(sketch, "E81", {"center": v(0, 120) * mm, "radius": 6 * mm});
            skArc(sketch, "E82", {"start": v(15, 120) * mm, "mid": v(0, 135) * mm, "end": v(-15, 120) * mm});
            skLineSegment(sketch, "E83", {"start": v(-15, 120) * mm, "end": v(-15, 108) * mm});
            skLineSegment(sketch, "E84", {"start": v(-15, 108) * mm, "end": v(-33, 90) * mm});
            skLineSegment(sketch, "E85.MirrorCS", {"start": v(15, 120) * mm, "end": v(15, 108) * mm});
            skLineSegment(sketch, "E86.MirrorCS", {"start": v(15, 108) * mm, "end": v(33, 90) * mm});
            skLineSegment(sketch, "E87", {"start": v(-80, 0) * mm, "end": v(80, 0) * mm, "construction": true});
            skLineSegment(sketch, "E88.MirrorCS", {"start": v(15, -108) * mm, "end": v(33, -90) * mm});
            skLineSegment(sketch, "E89.MirrorCS", {"start": v(15, -120) * mm, "end": v(15, -108) * mm});
            skCircle(sketch, "E90.MirrorC", {"center": v(0, -120) * mm, "radius": 6 * mm});
            skLineSegment(sketch, "E91.MirrorCS", {"start": v(-15, -120) * mm, "end": v(-15, -108) * mm});
            skArc(sketch, "E92.MirrorCS", {"start": v(15, -120) * mm, "mid": v(0, -135) * mm, "end": v(-15, -120) * mm});
            skLineSegment(sketch, "E93.MirrorCS", {"start": v(0, -90) * mm, "end": v(0, -120) * mm, "construction": true});
            skLineSegment(sketch, "E94.MirrorCS", {"start": v(-15, -108) * mm, "end": v(-33, -90) * mm});
            skSolve(sketch);
        }
        {
            var Q0;
            {var subQ1=sQuery(id+"F16.wireOp",EDGE,"E79.1");Q0=makeQuery(id+"F16.imprint","IMPRINT",FACE,{"disambiguationData":[TD([[makeQuery(id+"F16.imprint","IMPRINT",EDGE,{"derivedFrom":subQ1}),1.0]])]});}
            var Q1;
            Q1=makeQuery(id+"F16.imprint","IMPRINT",FACE,{"disambiguationData":[TD([[makeQuery(id+"F16.imprint","IMPRINT",EDGE,{"derivedFrom":sQuery(id+"F16.wireOp",EDGE,"E81")}),-1.0]])]});
            var Q2;
            {var subQ0=sQuery(id+"F16.wireOp",EDGE,"E88.MirrorCS");Q2=makeQuery(id+"F16.imprint","IMPRINT",FACE,{"disambiguationData":[TD([[makeQuery(id+"F16.imprint","IMPRINT",EDGE,{"derivedFrom":subQ0}),1.0]])]});}
            var Q3;
            Q3=makeQuery(id+"F2.opExtrude","CAP_FACE",FACE,{"disambiguationData":[OSD([sQuery(id+"F0.wireOp",EDGE,"E12"),sQuery(id+"F0.wireOp",EDGE,"E13"),sQuery(id+"F0.wireOp",EDGE,"E14"),sQuery(id+"F0.wireOp",EDGE,"E15"),sQuery(id+"F0.wireOp",EDGE,"E17.filletArc"),sQuery(id+"F0.wireOp",EDGE,"E18.filletArc"),sQuery(id+"F0.wireOp",EDGE,"E19.filletArc"),sQuery(id+"F0.wireOp",EDGE,"E20.filletArc"),sQuery(id+"F0.wireOp",EDGE,"E25.0"),sQuery(id+"F0.wireOp",EDGE,"E25.1"),sQuery(id+"F0.wireOp",EDGE,"E25.2"),sQuery(id+"F0.wireOp",EDGE,"E25.3"),sQuery(id+"F0.wireOp",EDGE,"E25.4"),sQuery(id+"F0.wireOp",EDGE,"E25.5"),sQuery(id+"F0.wireOp",EDGE,"E25.6"),sQuery(id+"F0.wireOp",EDGE,"E25.7")])],"isStart":false});
            extrude(context, id + "F17", {"entities" : qUnion([Q0, Q1, Q2]), "endBound" : BoundingType.UP_TO_SURFACE, "depth" : 25 * mm, "endBoundEntityFace" : qUnion([Q3]), "offsetDistance" : 25 * mm});
        }
    });
